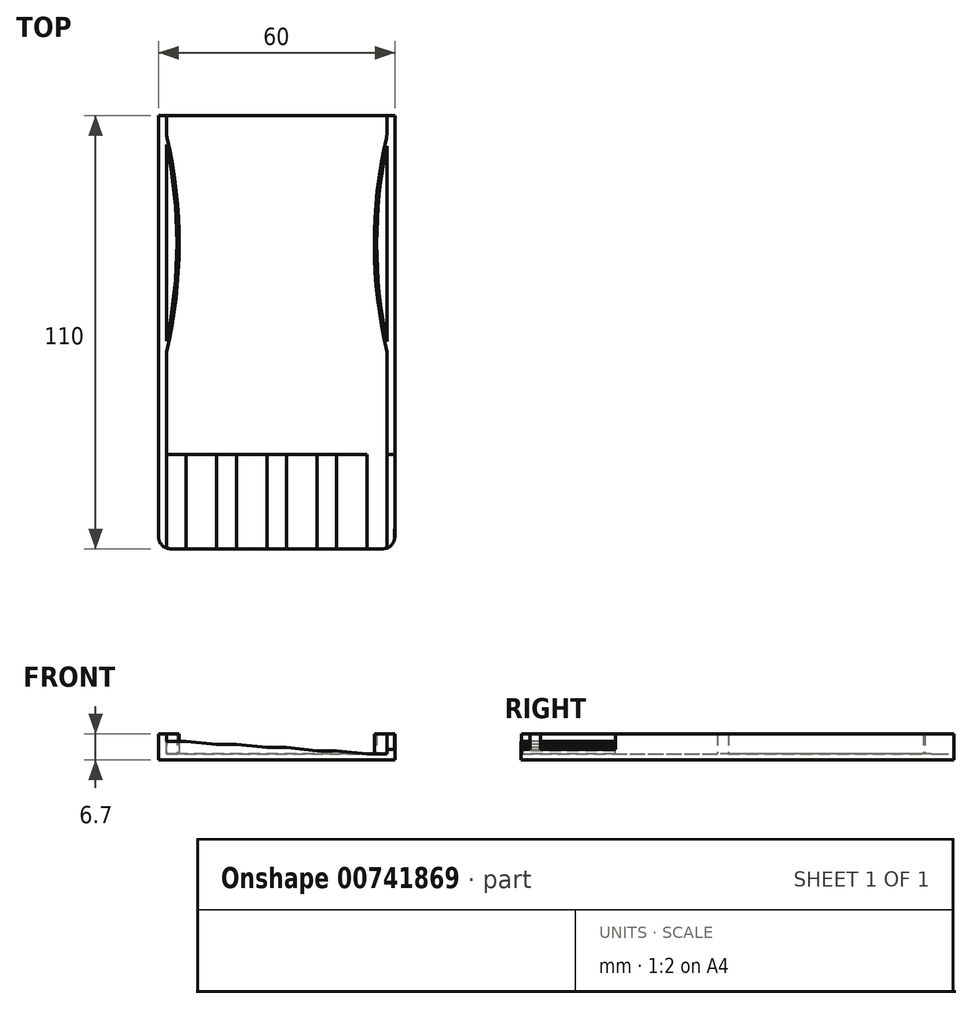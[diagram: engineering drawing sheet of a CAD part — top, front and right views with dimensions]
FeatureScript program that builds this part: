
annotation { "Feature Type Name" : "Feature", "Feature Type Description" : "" }
export const myFeature = defineFeature(function(context is Context, id is Id, definition is map)
    precondition{}
    {
        {
            var Q0;
            Q0=qCreatedBy(makeId("Top.planeOp"),FACE);
            var sketch = newSketch(context, id + "F0", { "sketchPlane" : qUnion([Q0])});
            skLineSegment(sketch, "E0.bottom", {"start": v(30, 55) * mm, "end": v(-30, 55) * mm});
            skLineSegment(sketch, "E0.top", {"start": v(30, -55) * mm, "end": v(-30, -55) * mm});
            skLineSegment(sketch, "E0.left", {"start": v(30, 55) * mm, "end": v(30, -55) * mm});
            skLineSegment(sketch, "E0.right", {"start": v(-30, 55) * mm, "end": v(-30, -55) * mm});
            skPoint(sketch, "E0.middle", {"position": v(0, 0) * mm});
            skSolve(sketch);
        }
        {
            var Q0;
            Q0=makeQuery(id+"F0.imprint","IMPRINT",FACE,{"disambiguationData":[TD([[makeQuery(id+"F0.imprint","IMPRINT",EDGE,{"derivedFrom":sQuery(id+"F0.wireOp",EDGE,"E0.bottom")}),1.0]])]});
            extrude(context, id + "F1", {"entities" : qUnion([Q0]), "depth" : 6.7 * mm, "offsetDistance" : 25 * mm});
        }
        {
            var Q0;
            Q0=makeQuery(id+"F1.opExtrude","CAP_FACE",FACE,{"disambiguationData":[OSD([sQuery(id+"F0.wireOp",EDGE,"E0.bottom"),sQuery(id+"F0.wireOp",EDGE,"E0.top"),sQuery(id+"F0.wireOp",EDGE,"E0.left"),sQuery(id+"F0.wireOp",EDGE,"E0.right")])],"isStart":false});
            var sketch = newSketch(context, id + "F2", { "sketchPlane" : qUnion([Q0])});
            skLineSegment(sketch, "E1.bottom", {"start": v(-28, -50) * mm, "end": v(28, -50) * mm});
            skLineSegment(sketch, "E1.top", {"start": v(-28, 55) * mm, "end": v(28, 55) * mm});
            skLineSegment(sketch, "E1.left", {"start": v(-28, -50) * mm, "end": v(-28, 55) * mm});
            skLineSegment(sketch, "E1.right", {"start": v(28, -50) * mm, "end": v(28, 55) * mm});
            skSolve(sketch);
        }
        {
            var Q0;
            Q0 = qSketchRegion(id + "F2", true);
            extrude(context, id + "F3", {"entities" : qUnion([Q0]), "operationType" : NewBodyOperationType.REMOVE, "oppositeDirection" : true, "depth" : 5.1 * mm, "offsetDistance" : 25 * mm});
        }
        {
            var Q0;
            Q0=makeQuery(id+"F3.boolean.opBoolean","COPY",FACE,{"derivedFrom":makeQuery(id+"F3.opExtrude","CAP_FACE",FACE,{"disambiguationData":[OSD([sQuery(id+"F2.wireOp",EDGE,"E1.bottom"),sQuery(id+"F2.wireOp",EDGE,"E1.top"),sQuery(id+"F2.wireOp",EDGE,"E1.left"),sQuery(id+"F2.wireOp",EDGE,"E1.right")])],"isStart":false})});
            var sketch = newSketch(context, id + "F4", { "sketchPlane" : qUnion([Q0])});
            skArc(sketch, "E2", {"start": v(-28, -5) * mm, "mid": v(-24.8, 22.5) * mm, "end": v(-28, 50) * mm});
            skArc(sketch, "E3", {"start": v(28, 50) * mm, "mid": v(24.8, 22.5) * mm, "end": v(28, -5) * mm});
            skArc(sketch, "E4", {"start": v(28, 47.33) * mm, "mid": v(25.4, 22.52) * mm, "end": v(28, -2.3) * mm});
            skArc(sketch, "E5", {"start": v(-28, -2.28) * mm, "mid": v(-25.37, 22.7) * mm, "end": v(-28, 47.68) * mm});
            skLineSegment(sketch, "E6", {"start": v(28, 50) * mm, "end": v(28, 47.33) * mm});
            skLineSegment(sketch, "E7", {"start": v(28, -2.3) * mm, "end": v(28, -5) * mm});
            skLineSegment(sketch, "E8", {"start": v(-28, 50) * mm, "end": v(-28, 47.68) * mm});
            skLineSegment(sketch, "E9", {"start": v(-28, -2.28) * mm, "end": v(-28, -5) * mm});
            skSolve(sketch);
        }
        {
            var Q0;
            Q0 = qSketchRegion(id + "F4", true);
            extrude(context, id + "F5", {"entities" : qUnion([Q0]), "operationType" : NewBodyOperationType.ADD, "depth" : 5.1 * mm, "offsetDistance" : 25 * mm});
        }
        {
            var Q0;
            Q0=makeQuery(id+"F1.opExtrude","SWEPT_EDGE",EDGE,{"disambiguationData":[OSD([sQuery(id+"F0.wireOp",EDGE,"E0.top"),sQuery(id+"F0.wireOp",EDGE,"E0.right")])]});
            var Q1;
            Q1=makeQuery(id+"F1.opExtrude","SWEPT_EDGE",EDGE,{"disambiguationData":[OSD([sQuery(id+"F0.wireOp",EDGE,"E0.top"),sQuery(id+"F0.wireOp",EDGE,"E0.left")])]});
            fillet(context, id + "F6", {"entities" : qUnion([Q0, Q1]), "radius" : 3 * mm, "tangentPropagation" : true, "allowEdgeOverflow" : false});
        }
        {
            var Q0;
            Q0=makeQuery(id+"F5.opExtrude","SWEPT_EDGE",EDGE,{"disambiguationData":[OSD([sQuery(id+"F2.wireOp",EDGE,"E1.right"),sQuery(id+"F4.wireOp",EDGE,"E3"),sQuery(id+"F4.wireOp",EDGE,"E7")])]});
            var Q1;
            Q1=makeQuery(id+"F5.opExtrude","SWEPT_EDGE",EDGE,{"disambiguationData":[OSD([sQuery(id+"F2.wireOp",EDGE,"E1.left"),sQuery(id+"F4.wireOp",EDGE,"E2"),sQuery(id+"F4.wireOp",EDGE,"E9")])]});
            var Q2;
            Q2=makeQuery(id+"F5.opExtrude","SWEPT_EDGE",EDGE,{"disambiguationData":[OSD([sQuery(id+"F2.wireOp",EDGE,"E1.left"),sQuery(id+"F4.wireOp",EDGE,"E2"),sQuery(id+"F4.wireOp",EDGE,"E8")])]});
            var Q3;
            Q3=makeQuery(id+"F5.opExtrude","SWEPT_EDGE",EDGE,{"disambiguationData":[OSD([sQuery(id+"F2.wireOp",EDGE,"E1.right"),sQuery(id+"F4.wireOp",EDGE,"E3"),sQuery(id+"F4.wireOp",EDGE,"E6")])]});
            fillet(context, id + "F7", {"entities" : qUnion([Q0, Q1, Q2, Q3]), "radius" : 6 * mm, "tangentPropagation" : true, "allowEdgeOverflow" : false});
        }
        {
            var Q0;
            Q0=makeQuery(id+"F3.boolean.opBoolean","COPY",FACE,{"derivedFrom":makeQuery(id+"F3.opExtrude","SWEPT_FACE",FACE,{"disambiguationData":[OSD([sQuery(id+"F2.wireOp",EDGE,"E1.bottom")])]})});
            var sketch = newSketch(context, id + "F8", { "sketchPlane" : qUnion([Q0])});
            skLineSegment(sketch, "E10", {"start": v(-23, 1.6) * mm, "end": v(-15.25, 2.4) * mm});
            skLineSegment(sketch, "E11", {"start": v(-15.25, 2.4) * mm, "end": v(-10.25, 2.4) * mm});
            skLineSegment(sketch, "E12", {"start": v(-10.25, 2.4) * mm, "end": v(-2.5, 3.2) * mm});
            skLineSegment(sketch, "E13", {"start": v(-2.5, 3.2) * mm, "end": v(2.5, 3.2) * mm});
            skLineSegment(sketch, "E14", {"start": v(2.5, 3.2) * mm, "end": v(10.25, 4) * mm});
            skLineSegment(sketch, "E15", {"start": v(10.25, 4) * mm, "end": v(15.25, 4) * mm});
            skLineSegment(sketch, "E16", {"start": v(15.25, 4) * mm, "end": v(23, 4.8) * mm});
            skLineSegment(sketch, "E17", {"start": v(23, 4.8) * mm, "end": v(28, 4.8) * mm});
            skLineSegment(sketch, "E18", {"start": v(28, 4.8) * mm, "end": v(28, 1.6) * mm});
            skLineSegment(sketch, "E19", {"start": v(28, 1.6) * mm, "end": v(-23, 1.6) * mm});
            skSolve(sketch);
        }
        {
            var Q0;
            Q0 = qSketchRegion(id + "F8", true);
            extrude(context, id + "F9", {"entities" : qUnion([Q0]), "operationType" : NewBodyOperationType.ADD, "depth" : 19 * mm, "offsetDistance" : 25 * mm});
        }
        {
            var Q0;
            Q0=makeQuery(id+"F5.boolean.opBoolean","MERGE",FACE,{"derivedFrom":[makeQuery(id+"F1.opExtrude","CAP_FACE",FACE,{"disambiguationData":[OSD([sQuery(id+"F0.wireOp",EDGE,"E0.bottom"),sQuery(id+"F0.wireOp",EDGE,"E0.top"),sQuery(id+"F0.wireOp",EDGE,"E0.left"),sQuery(id+"F0.wireOp",EDGE,"E0.right")])],"isStart":false}),makeQuery(id+"F5.opExtrude","CAP_FACE",FACE,{"disambiguationData":[OSD([sQuery(id+"F4.wireOp",EDGE,"E2"),sQuery(id+"F4.wireOp",EDGE,"E5"),sQuery(id+"F4.wireOp",EDGE,"E8"),sQuery(id+"F4.wireOp",EDGE,"E9")])],"isStart":false}),makeQuery(id+"F5.opExtrude","CAP_FACE",FACE,{"disambiguationData":[OSD([sQuery(id+"F4.wireOp",EDGE,"E3"),sQuery(id+"F4.wireOp",EDGE,"E4"),sQuery(id+"F4.wireOp",EDGE,"E6"),sQuery(id+"F4.wireOp",EDGE,"E7")])],"isStart":false})]});
            var sketch = newSketch(context, id + "F10", { "sketchPlane" : qUnion([Q0])});
            skLineSegment(sketch, "E20.bottom", {"start": v(28, -31) * mm, "end": v(30, -31) * mm});
            skLineSegment(sketch, "E20.top", {"start": v(28, -50) * mm, "end": v(30, -50) * mm});
            skLineSegment(sketch, "E20.left", {"start": v(28, -31) * mm, "end": v(28, -50) * mm});
            skLineSegment(sketch, "E20.right", {"start": v(30, -31) * mm, "end": v(30, -50) * mm});
            skSolve(sketch);
        }
        {
            var Q0;
            Q0 = qSketchRegion(id + "F10", true);
            extrude(context, id + "F11", {"entities" : qUnion([Q0]), "operationType" : NewBodyOperationType.REMOVE, "oppositeDirection" : true, "depth" : 4 * mm, "offsetDistance" : 25 * mm});
        }
        {
            var Q0;
            Q0=makeQuery(id+"F11.boolean.opBoolean","MERGE",FACE,{"derivedFrom":[makeQuery(id+"F3.boolean.opBoolean","COPY",FACE,{"derivedFrom":makeQuery(id+"F3.opExtrude","SWEPT_FACE",FACE,{"disambiguationData":[OSD([sQuery(id+"F2.wireOp",EDGE,"E1.bottom")])]})}),makeQuery(id+"F11.opExtrude","SWEPT_FACE",FACE,{"disambiguationData":[OSD([sQuery(id+"F10.wireOp",EDGE,"E20.top")])]})]});
            var sketch = newSketch(context, id + "F12", { "sketchPlane" : qUnion([Q0])});
            skLineSegment(sketch, "E21", {"start": v(28, 4.8) * mm, "end": v(23, 4.8) * mm});
            skLineSegment(sketch, "E22", {"start": v(23, 4.8) * mm, "end": v(15.25, 4) * mm});
            skLineSegment(sketch, "E23", {"start": v(15.25, 4) * mm, "end": v(10.25, 4) * mm});
            skLineSegment(sketch, "E24", {"start": v(10.25, 4) * mm, "end": v(2.5, 3.2) * mm});
            skLineSegment(sketch, "E25", {"start": v(2.5, 3.2) * mm, "end": v(-2.5, 3.2) * mm});
            skLineSegment(sketch, "E26", {"start": v(-2.5, 3.2) * mm, "end": v(-10.25, 2.4) * mm});
            skLineSegment(sketch, "E27", {"start": v(-10.25, 2.4) * mm, "end": v(-15.25, 2.4) * mm});
            skLineSegment(sketch, "E28", {"start": v(-15.25, 2.4) * mm, "end": v(-23, 1.6) * mm});
            skLineSegment(sketch, "E29", {"start": v(-23, 1.6) * mm, "end": v(-28, 1.6) * mm});
            skLineSegment(sketch, "E30", {"start": v(-28, 1.6) * mm, "end": v(-28, 2.7) * mm});
            skLineSegment(sketch, "E31", {"start": v(-28, 2.7) * mm, "end": v(-29.92, 2.7) * mm});
            skLineSegment(sketch, "E32", {"start": v(-29.92, 2.7) * mm, "end": v(-29.92, 6.7) * mm});
            skLineSegment(sketch, "E33", {"start": v(-29.92, 6.7) * mm, "end": v(28, 6.7) * mm});
            skLineSegment(sketch, "E34", {"start": v(28, 6.7) * mm, "end": v(28, 4.8) * mm});
            skSolve(sketch);
        }
        {
            var Q0;
            Q0 = qSketchRegion(id + "F12", true);
            extrude(context, id + "F13", {"entities" : qUnion([Q0]), "operationType" : NewBodyOperationType.REMOVE, "oppositeDirection" : true, "depth" : 25 * mm, "offsetDistance" : 25 * mm});
        }
    });
